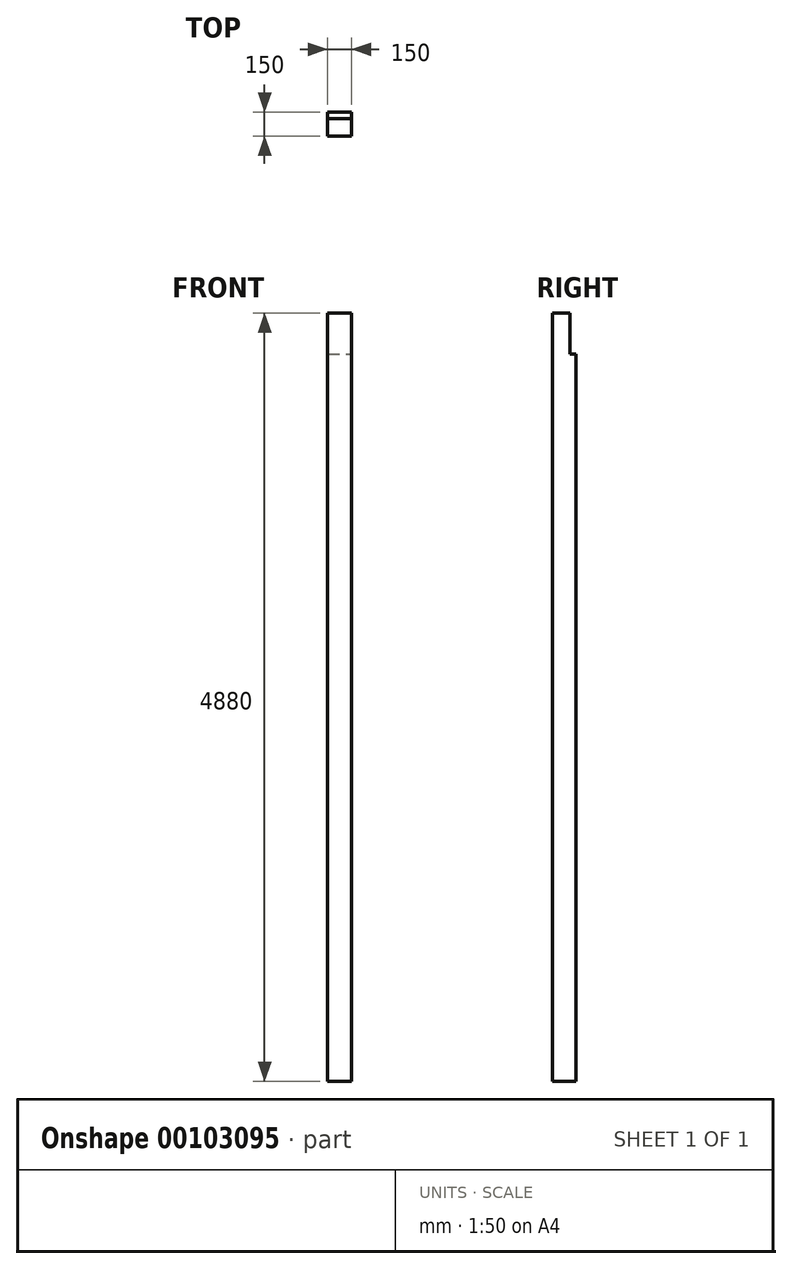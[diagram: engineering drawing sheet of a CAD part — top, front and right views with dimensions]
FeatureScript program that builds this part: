
annotation { "Feature Type Name" : "Feature", "Feature Type Description" : "" }
export const myFeature = defineFeature(function(context is Context, id is Id, definition is map)
    precondition{}
    {
        {
            var Q0;
            Q0=qCreatedBy(makeId("Top.planeOp"),FACE);
            var sketch = newSketch(context, id + "F0", { "sketchPlane" : qUnion([Q0])});
            skLineSegment(sketch, "E0.bottom", {"start": v(-75, 75) * mm, "end": v(75, 75) * mm});
            skLineSegment(sketch, "E0.top", {"start": v(-75, -75) * mm, "end": v(75, -75) * mm});
            skLineSegment(sketch, "E0.left", {"start": v(-75, 75) * mm, "end": v(-75, -75) * mm});
            skLineSegment(sketch, "E0.right", {"start": v(75, 75) * mm, "end": v(75, -75) * mm});
            skPoint(sketch, "E0.middle", {"position": v(0, 0) * mm});
            skSolve(sketch);
        }
        {
            var Q0;
            Q0=makeQuery(id+"F0.imprint","IMPRINT",FACE,{"disambiguationData":[TD([[makeQuery(id+"F0.imprint","IMPRINT",EDGE,{"derivedFrom":sQuery(id+"F0.wireOp",EDGE,"E0.bottom")}),-1.0]])]});
            extrude(context, id + "F1", {"entities" : qUnion([Q0]), "depth" : 4880 * mm});
        }
        {
            var Q0;
            Q0=makeQuery(id+"F1.opExtrude","CAP_FACE",FACE,{"disambiguationData":[OSD([sQuery(id+"F0.wireOp",EDGE,"E0.bottom"),sQuery(id+"F0.wireOp",EDGE,"E0.top"),sQuery(id+"F0.wireOp",EDGE,"E0.left"),sQuery(id+"F0.wireOp",EDGE,"E0.right")])],"isStart":false});
            var sketch = newSketch(context, id + "F2", { "sketchPlane" : qUnion([Q0])});
            skLineSegment(sketch, "E1", {"start": v(75, -36) * mm, "end": v(-75, -36) * mm});
            skLineSegment(sketch, "E2", {"start": v(-75, 36) * mm, "end": v(75, 36) * mm});
            skLineSegment(sketch, "E3.top", {"start": v(-75, 75) * mm, "end": v(75, 75) * mm});
            skLineSegment(sketch, "E3.left", {"start": v(-75, 36) * mm, "end": v(-75, 75) * mm});
            skLineSegment(sketch, "E3.right", {"start": v(75, 36) * mm, "end": v(75, 75) * mm});
            skLineSegment(sketch, "E4.bottom", {"start": v(-75, -36) * mm, "end": v(75, -36) * mm});
            skLineSegment(sketch, "E4.top", {"start": v(-75, -75) * mm, "end": v(75, -75) * mm});
            skLineSegment(sketch, "E4.left", {"start": v(-75, -36) * mm, "end": v(-75, -75) * mm});
            skLineSegment(sketch, "E4.right", {"start": v(75, -36) * mm, "end": v(75, -75) * mm});
            skSolve(sketch);
        }
        {
            var Q0;
            Q0=makeQuery(id+"F2.imprint","IMPRINT",FACE,{"disambiguationData":[TD([[makeQuery(id+"F2.imprint","IMPRINT",EDGE,{"derivedFrom":sQuery(id+"F2.wireOp",EDGE,"E2")}),1.0]])]});
            var Q1;
            Q1=makeQuery(id+"F2.imprint","IMPRINT",FACE,{"disambiguationData":[TD([[makeQuery(id+"F2.imprint","IMPRINT",EDGE,{"derivedFrom":sQuery(id+"F2.wireOp",EDGE,"E4.bottom")}),-1.0]])]});
            extrude(context, id + "F3", {"entities" : qUnion([Q0, Q1]), "operationType" : NewBodyOperationType.REMOVE, "oppositeDirection" : true, "depth" : 260 * mm});
        }
        {
            var Q0;
            Q0=makeQuery(id+"F2.imprint","IMPRINT",FACE,{"disambiguationData":[TD([[makeQuery(id+"F2.imprint","IMPRINT",EDGE,{"derivedFrom":sQuery(id+"F2.wireOp",EDGE,"E2")}),1.0]])]});
            extrude(context, id + "F4", {"entities" : qUnion([Q0]), "operationType" : NewBodyOperationType.REMOVE, "oppositeDirection" : true, "depth" : 260 * mm});
        }
    });
